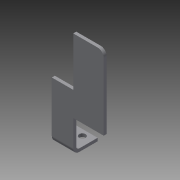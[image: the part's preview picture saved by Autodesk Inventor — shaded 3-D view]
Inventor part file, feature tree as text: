
AUTODESK INVENTOR PART (.ipt)
format: ipt  version: 2013 (Build 170138000, 138)  size: 114,688 bytes
history: native  units: in
note: dims shown in document units (in); Inventor stores cm internally (conversion verified against a paired STEP export)
features: sheet_metal_op x4, sketch x4, other x3, extrude x1, reference x1
ambient origin geometry x8: Origin, YZ Plane, XZ Plane, XY Plane, X Axis, Y Axis, Z Axis, Center Point
bodies: Solid1 (feature_tree)
feature tree (13):
  sheet_metal_op  "Face1"
  sheet_metal_op  "Flange1"
  extrude  "Extrusion1"  Depth=0.125in
  sketch  "Sketch1"  dims[d0=0.125in d1=0.125in]
  other  "Plate1"
  sketch  "Sketch2"  dims[d2=0.0625in]
  other  "Plate2"
  sheet_metal_op  "Bend1"
  sheet_metal_op  "Corner1"
  sketch  "Sketch3"  dims[d3=0.25in]
  reference  "Reference1"
  sketch  "Sketch5"  dims[d4=0.125in d5=1.25in d6=90.0deg d7=0.125in d8=0.5in d9=0.125in d10=0.125in d11=0.125in d12=0.0in d13=1.5in d14=1.5in d15=0.0in]
  other  "Cut1"
